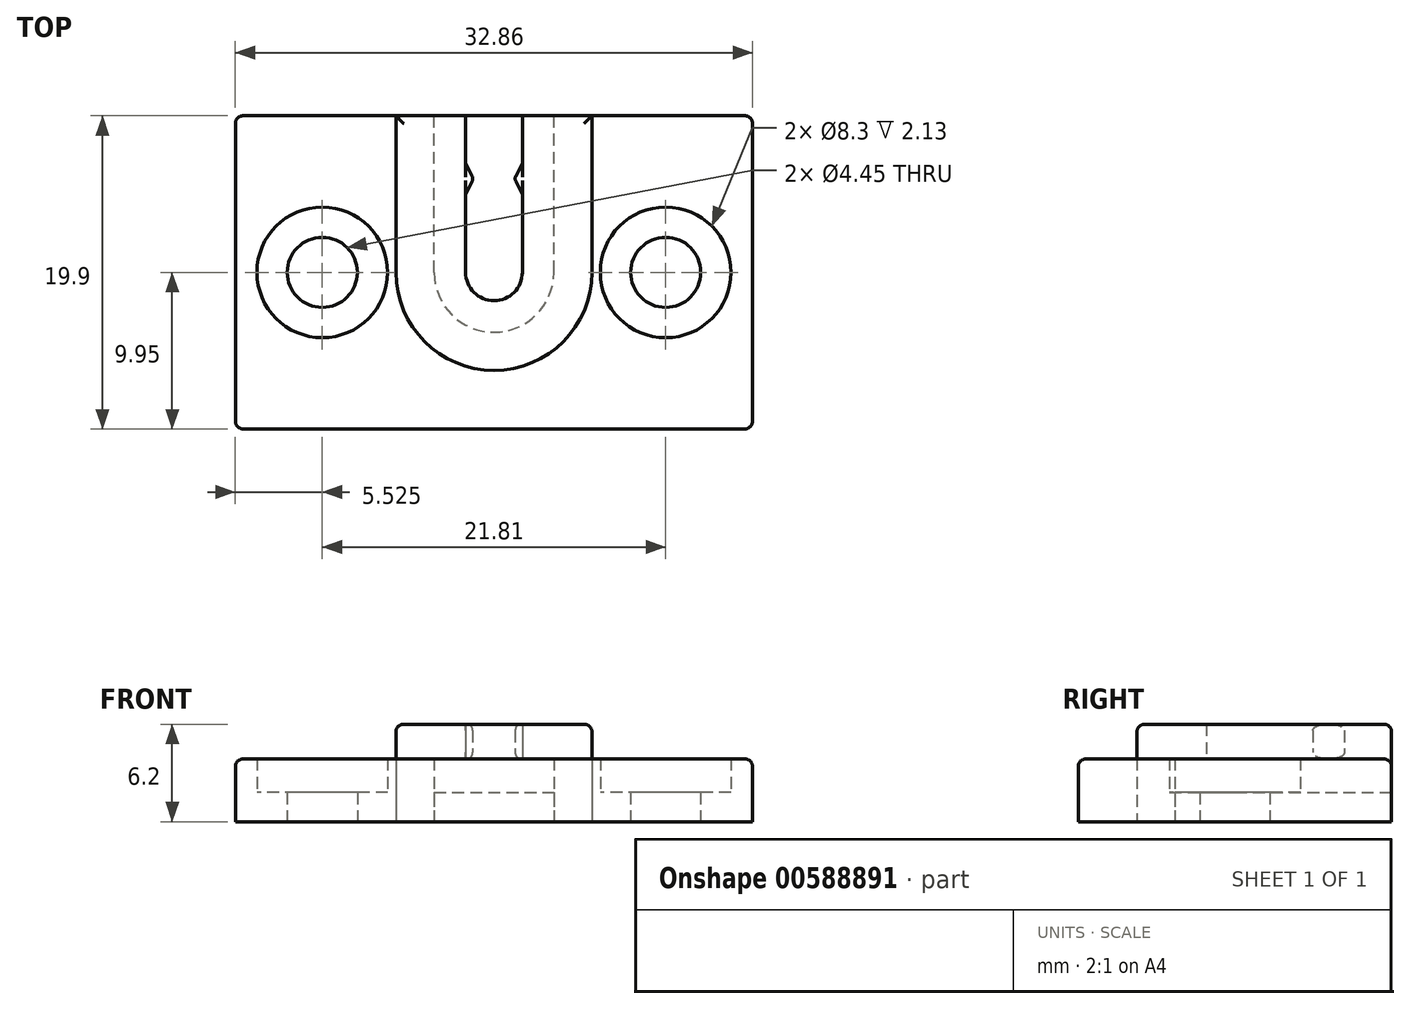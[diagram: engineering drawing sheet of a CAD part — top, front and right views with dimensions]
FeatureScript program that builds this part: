
annotation { "Feature Type Name" : "Feature", "Feature Type Description" : "" }
export const myFeature = defineFeature(function(context is Context, id is Id, definition is map)
    precondition{}
    {
        {
            var Q0;
            Q0=qCreatedBy(makeId("Top.planeOp"),FACE);
            var sketch = newSketch(context, id + "F0", { "sketchPlane" : qUnion([Q0])});
            skLineSegment(sketch, "E0.bottom", {"start": v(-16.43, 9.95) * mm, "end": v(16.43, 9.95) * mm});
            skLineSegment(sketch, "E0.top", {"start": v(-16.43, -9.95) * mm, "end": v(16.43, -9.95) * mm});
            skLineSegment(sketch, "E0.left", {"start": v(-16.43, 9.95) * mm, "end": v(-16.43, -9.95) * mm});
            skLineSegment(sketch, "E0.right", {"start": v(16.43, 9.95) * mm, "end": v(16.43, -9.95) * mm});
            skPoint(sketch, "E1", {"position": v(0, 9.95) * mm});
            skPoint(sketch, "E2", {"position": v(-16.43, 0) * mm});
            skLineSegment(sketch, "E3", {"start": v(-16.43, 9.95) * mm, "end": v(16.43, -9.95) * mm, "construction": true});
            skPoint(sketch, "E4", {"position": v(0, 0) * mm});
            skCircle(sketch, "E5", {"center": v(-10.9, 0) * mm, "radius": 4.15 * mm});
            skCircle(sketch, "E6", {"center": v(-10.9, 0) * mm, "radius": 2.23 * mm});
            skCircle(sketch, "E7", {"center": v(10.9, 0) * mm, "radius": 4.15 * mm});
            skLineSegment(sketch, "E8", {"start": v(-15.06, 0) * mm, "end": v(-16.43, 0) * mm, "construction": true});
            skLineSegment(sketch, "E9", {"start": v(16.43, 0) * mm, "end": v(15.06, 0) * mm, "construction": true});
            skCircle(sketch, "E10", {"center": v(10.9, 0) * mm, "radius": 2.23 * mm});
            skCircle(sketch, "E11", {"center": v(0, 0) * mm, "radius": 1.8 * mm});
            skCircle(sketch, "E12", {"center": v(0, 0) * mm, "radius": 6.22 * mm});
            skPoint(sketch, "E13", {"position": v(-6.22, 0) * mm});
            skPoint(sketch, "E14", {"position": v(6.22, 0) * mm});
            skPoint(sketch, "E15", {"position": v(-1.8, 0) * mm});
            skPoint(sketch, "E16", {"position": v(1.8, 0) * mm});
            skCircle(sketch, "E17", {"center": v(0, 0) * mm, "radius": 3.8 * mm});
            skPoint(sketch, "E18", {"position": v(-3.8, 0) * mm});
            skPoint(sketch, "E19", {"position": v(3.8, 0) * mm});
            skLineSegment(sketch, "E20", {"start": v(-6.22, 0) * mm, "end": v(-6.22, 9.95) * mm});
            skLineSegment(sketch, "E21", {"start": v(6.22, 0) * mm, "end": v(6.22, 9.95) * mm});
            skLineSegment(sketch, "E22", {"start": v(-3.8, 0) * mm, "end": v(-3.8, 9.95) * mm});
            skLineSegment(sketch, "E23", {"start": v(3.8, 0) * mm, "end": v(3.8, 9.95) * mm});
            skLineSegment(sketch, "E24", {"start": v(-1.8, 0) * mm, "end": v(-1.8, 9.95) * mm});
            skLineSegment(sketch, "E25", {"start": v(1.8, 0) * mm, "end": v(1.8, 9.95) * mm});
            skPoint(sketch, "E26", {"position": v(-1.8, 6.95) * mm});
            skPoint(sketch, "E27", {"position": v(-1.8, 4.95) * mm});
            skLineSegment(sketch, "E28", {"start": v(-1.8, 6.95) * mm, "end": v(-1.3, 5.95) * mm});
            skLineSegment(sketch, "E29", {"start": v(-1.3, 5.95) * mm, "end": v(-1.8, 4.95) * mm});
            skLineSegment(sketch, "E30", {"start": v(1.8, 6.95) * mm, "end": v(1.3, 5.95) * mm});
            skLineSegment(sketch, "E31", {"start": v(1.3, 5.95) * mm, "end": v(1.8, 4.95) * mm});
            skSolve(sketch);
        }
        {
            var Q0;
            Q0=makeQuery(id+"F0.imprint","IMPRINT",FACE,{"disambiguationData":[TD([[makeQuery(id+"F0.imprint","IMPRINT",EDGE,{"derivedFrom":sQuery(id+"F0.wireOp",EDGE,"E0.top")}),1.0]])]});
            extrude(context, id + "F1", {"entities" : qUnion([Q0]), "depth" : 4 * mm, "offsetDistance" : 25 * mm});
        }
        {
            var Q0;
            Q0=makeQuery(id+"F0.imprint","IMPRINT",FACE,{"disambiguationData":[TD([[makeQuery(id+"F0.imprint","IMPRINT",EDGE,{"derivedFrom":sQuery(id+"F0.wireOp",EDGE,"E5")}),1.0]])]});
            var Q1;
            Q1=makeQuery(id+"F0.imprint","IMPRINT",FACE,{"disambiguationData":[TD([[makeQuery(id+"F0.imprint","IMPRINT",EDGE,{"derivedFrom":sQuery(id+"F0.wireOp",EDGE,"E7")}),1.0]])]});
            var Q2;
            {var subQ0=sQuery(id+"F0.wireOp",EDGE,"E24");var subQ6=sQuery(id+"F0.wireOp",EDGE,"E12");var subQ8=makeQuery(id+"F0.imprint","INTERSECT",VERTEX,{"derivedFrom":[subQ6,subQ0]});Q2=makeQuery(id+"F0.imprint","IMPRINT",FACE,{"disambiguationData":[TD([[makeQuery(id+"F0.imprint","IMPRINT",EDGE,{"disambiguationData":[TD([[subQ8,-1.0]])],"derivedFrom":subQ6}),1.0]])]});}
            var Q3;
            {var subQ0=sQuery(id+"F0.wireOp",EDGE,"E24");var subQ1=sQuery(id+"F0.wireOp",EDGE,"E11");var subQ2=makeQuery(id+"F0.imprint","INTERSECT",VERTEX,{"derivedFrom":[subQ1,subQ0]});Q3=makeQuery(id+"F0.imprint","IMPRINT",FACE,{"disambiguationData":[TD([[makeQuery(id+"F0.imprint","IMPRINT",EDGE,{"disambiguationData":[TD([[subQ2,1.0]])],"derivedFrom":subQ1}),-1.0]])]});}
            var Q4;
            {var subQ3=sQuery(id+"F0.wireOp",EDGE,"E24");var subQ5=sQuery(id+"F0.wireOp",EDGE,"E11");var subQ6=makeQuery(id+"F0.imprint","INTERSECT",VERTEX,{"derivedFrom":[subQ5,subQ3]});Q4=makeQuery(id+"F0.imprint","IMPRINT",FACE,{"disambiguationData":[TD([[makeQuery(id+"F0.imprint","IMPRINT",EDGE,{"disambiguationData":[TD([[subQ6,-1.0]])],"derivedFrom":subQ5}),-1.0]])]});}
            var Q5;
            {var subQ0=sQuery(id+"F0.wireOp",EDGE,"E11");var subQ1=makeQuery(id+"F0.imprint","INTERSECT",VERTEX,{"derivedFrom":[subQ0,sQuery(id+"F0.wireOp",EDGE,"E24")]});Q5=makeQuery(id+"F0.imprint","IMPRINT",FACE,{"disambiguationData":[TD([[makeQuery(id+"F0.imprint","IMPRINT",EDGE,{"disambiguationData":[TD([[subQ1,1.0]])],"derivedFrom":subQ0}),1.0]])]});}
            var Q6;
            {var subQ4=sQuery(id+"F0.wireOp",EDGE,"E29");Q6=makeQuery(id+"F0.imprint","IMPRINT",FACE,{"disambiguationData":[TD([[makeQuery(id+"F0.imprint","IMPRINT",EDGE,{"derivedFrom":subQ4}),1.0]])]});}
            var Q7;
            {var subQ6=sQuery(id+"F0.wireOp",EDGE,"E0.bottom");var subQ9=sQuery(id+"F0.wireOp",EDGE,"E24");var subQ10=makeQuery(id+"F0.imprint","INTERSECT",VERTEX,{"derivedFrom":[subQ6,subQ9]});Q7=makeQuery(id+"F0.imprint","IMPRINT",FACE,{"disambiguationData":[TD([[makeQuery(id+"F0.imprint","IMPRINT",EDGE,{"disambiguationData":[TD([[subQ10,-1.0]])],"derivedFrom":subQ6}),-1.0]])]});}
            var Q8;
            {var subQ0=sQuery(id+"F0.wireOp",EDGE,"E22");var subQ1=sQuery(id+"F0.wireOp",EDGE,"E0.bottom");var subQ2=makeQuery(id+"F0.imprint","INTERSECT",VERTEX,{"derivedFrom":[subQ1,subQ0]});Q8=makeQuery(id+"F0.imprint","IMPRINT",FACE,{"disambiguationData":[TD([[makeQuery(id+"F0.imprint","IMPRINT",EDGE,{"disambiguationData":[TD([[subQ2,-1.0]])],"derivedFrom":subQ1}),-1.0]])]});}
            var Q9;
            {var subQ0=sQuery(id+"F0.wireOp",EDGE,"E23");var subQ1=sQuery(id+"F0.wireOp",EDGE,"E0.bottom");var subQ2=makeQuery(id+"F0.imprint","INTERSECT",VERTEX,{"derivedFrom":[subQ1,subQ0]});Q9=makeQuery(id+"F0.imprint","IMPRINT",FACE,{"disambiguationData":[TD([[makeQuery(id+"F0.imprint","IMPRINT",EDGE,{"disambiguationData":[TD([[subQ2,1.0]])],"derivedFrom":subQ1}),-1.0]])]});}
            var Q10;
            {var subQ4=sQuery(id+"F0.wireOp",EDGE,"E23");var subQ6=sQuery(id+"F0.wireOp",EDGE,"E12");var subQ7=makeQuery(id+"F0.imprint","INTERSECT",VERTEX,{"derivedFrom":[subQ6,subQ4]});Q10=makeQuery(id+"F0.imprint","IMPRINT",FACE,{"disambiguationData":[TD([[makeQuery(id+"F0.imprint","IMPRINT",EDGE,{"disambiguationData":[TD([[subQ7,-1.0]])],"derivedFrom":subQ6}),1.0]])]});}
            var Q11;
            {var subQ5=sQuery(id+"F0.wireOp",EDGE,"E31");Q11=makeQuery(id+"F0.imprint","IMPRINT",FACE,{"disambiguationData":[TD([[makeQuery(id+"F0.imprint","IMPRINT",EDGE,{"derivedFrom":subQ5}),1.0]])]});}
            var Q12;
            {var subQ0=sQuery(id+"F0.wireOp",EDGE,"E25");var subQ1=sQuery(id+"F0.wireOp",EDGE,"E12");var subQ2=makeQuery(id+"F0.imprint","INTERSECT",VERTEX,{"derivedFrom":[subQ1,subQ0]});Q12=makeQuery(id+"F0.imprint","IMPRINT",FACE,{"disambiguationData":[TD([[makeQuery(id+"F0.imprint","IMPRINT",EDGE,{"disambiguationData":[TD([[subQ2,-1.0]])],"derivedFrom":subQ1}),-1.0]])]});}
            var Q13;
            {var subQ0=sQuery(id+"F0.wireOp",EDGE,"E28");var subQ1=sQuery(id+"F0.wireOp",EDGE,"E12");var subQ2=makeQuery(id+"F0.imprint","INTERSECT",VERTEX,{"derivedFrom":[subQ1,subQ0]});Q13=makeQuery(id+"F0.imprint","IMPRINT",FACE,{"disambiguationData":[TD([[makeQuery(id+"F0.imprint","IMPRINT",EDGE,{"disambiguationData":[TD([[subQ2,-1.0]])],"derivedFrom":subQ1}),-1.0]])]});}
            var Q14;
            {var subQ5=sQuery(id+"F0.wireOp",EDGE,"E29");Q14=makeQuery(id+"F0.imprint","IMPRINT",FACE,{"disambiguationData":[TD([[makeQuery(id+"F0.imprint","IMPRINT",EDGE,{"derivedFrom":subQ5}),-1.0]])]});}
            extrude(context, id + "F2", {"entities" : qUnion([Q0, Q1, Q2, Q3, Q4, Q5, Q6, Q7, Q8, Q9, Q10, Q11, Q12, Q13, Q14]), "operationType" : NewBodyOperationType.ADD, "depth" : 1.87 * mm, "offsetDistance" : 25 * mm});
        }
        {
            var Q0;
            {var subQ0=sQuery(id+"F0.wireOp",EDGE,"E20");Q0=makeQuery(id+"F0.imprint","IMPRINT",FACE,{"disambiguationData":[TD([[makeQuery(id+"F0.imprint","IMPRINT",EDGE,{"derivedFrom":subQ0}),-1.0]])]});}
            var Q1;
            {var subQ0=sQuery(id+"F0.wireOp",EDGE,"E12");var subQ2=makeQuery(id+"F0.imprint","INTERSECT",VERTEX,{"derivedFrom":[subQ0,sQuery(id+"F0.wireOp",EDGE,"E21")]});Q1=makeQuery(id+"F0.imprint","IMPRINT",FACE,{"disambiguationData":[TD([[makeQuery(id+"F0.imprint","IMPRINT",EDGE,{"disambiguationData":[TD([[subQ2,-1.0]])],"derivedFrom":subQ0}),1.0]])]});}
            var Q2;
            {var subQ0=sQuery(id+"F0.wireOp",EDGE,"E21");Q2=makeQuery(id+"F0.imprint","IMPRINT",FACE,{"disambiguationData":[TD([[makeQuery(id+"F0.imprint","IMPRINT",EDGE,{"derivedFrom":subQ0}),1.0]])]});}
            extrude(context, id + "F3", {"entities" : qUnion([Q0, Q1, Q2]), "depth" : 6.2 * mm, "offsetDistance" : 25 * mm});
        }
        {
            var Q0;
            {var subQ0=sQuery(id+"F0.wireOp",EDGE,"E22");var subQ1=sQuery(id+"F0.wireOp",EDGE,"E0.bottom");var subQ2=makeQuery(id+"F0.imprint","INTERSECT",VERTEX,{"derivedFrom":[subQ1,subQ0]});Q0=makeQuery(id+"F0.imprint","IMPRINT",FACE,{"disambiguationData":[TD([[makeQuery(id+"F0.imprint","IMPRINT",EDGE,{"disambiguationData":[TD([[subQ2,-1.0]])],"derivedFrom":subQ1}),-1.0]])]});}
            var Q1;
            {var subQ0=sQuery(id+"F0.wireOp",EDGE,"E24");var subQ6=sQuery(id+"F0.wireOp",EDGE,"E12");var subQ8=makeQuery(id+"F0.imprint","INTERSECT",VERTEX,{"derivedFrom":[subQ6,subQ0]});Q1=makeQuery(id+"F0.imprint","IMPRINT",FACE,{"disambiguationData":[TD([[makeQuery(id+"F0.imprint","IMPRINT",EDGE,{"disambiguationData":[TD([[subQ8,-1.0]])],"derivedFrom":subQ6}),1.0]])]});}
            var Q2;
            {var subQ3=sQuery(id+"F0.wireOp",EDGE,"E24");var subQ5=sQuery(id+"F0.wireOp",EDGE,"E11");var subQ6=makeQuery(id+"F0.imprint","INTERSECT",VERTEX,{"derivedFrom":[subQ5,subQ3]});Q2=makeQuery(id+"F0.imprint","IMPRINT",FACE,{"disambiguationData":[TD([[makeQuery(id+"F0.imprint","IMPRINT",EDGE,{"disambiguationData":[TD([[subQ6,-1.0]])],"derivedFrom":subQ5}),-1.0]])]});}
            var Q3;
            {var subQ4=sQuery(id+"F0.wireOp",EDGE,"E23");var subQ6=sQuery(id+"F0.wireOp",EDGE,"E12");var subQ7=makeQuery(id+"F0.imprint","INTERSECT",VERTEX,{"derivedFrom":[subQ6,subQ4]});Q3=makeQuery(id+"F0.imprint","IMPRINT",FACE,{"disambiguationData":[TD([[makeQuery(id+"F0.imprint","IMPRINT",EDGE,{"disambiguationData":[TD([[subQ7,-1.0]])],"derivedFrom":subQ6}),1.0]])]});}
            var Q4;
            {var subQ0=sQuery(id+"F0.wireOp",EDGE,"E23");var subQ1=sQuery(id+"F0.wireOp",EDGE,"E0.bottom");var subQ2=makeQuery(id+"F0.imprint","INTERSECT",VERTEX,{"derivedFrom":[subQ1,subQ0]});Q4=makeQuery(id+"F0.imprint","IMPRINT",FACE,{"disambiguationData":[TD([[makeQuery(id+"F0.imprint","IMPRINT",EDGE,{"disambiguationData":[TD([[subQ2,1.0]])],"derivedFrom":subQ1}),-1.0]])]});}
            var Q5;
            {var subQ0=sQuery(id+"F0.wireOp",EDGE,"E28");var subQ1=sQuery(id+"F0.wireOp",EDGE,"E12");var subQ2=makeQuery(id+"F0.imprint","INTERSECT",VERTEX,{"derivedFrom":[subQ1,subQ0]});Q5=makeQuery(id+"F0.imprint","IMPRINT",FACE,{"disambiguationData":[TD([[makeQuery(id+"F0.imprint","IMPRINT",EDGE,{"disambiguationData":[TD([[subQ2,-1.0]])],"derivedFrom":subQ1}),-1.0]])]});}
            var Q6;
            {var subQ5=sQuery(id+"F0.wireOp",EDGE,"E29");Q6=makeQuery(id+"F0.imprint","IMPRINT",FACE,{"disambiguationData":[TD([[makeQuery(id+"F0.imprint","IMPRINT",EDGE,{"derivedFrom":subQ5}),-1.0]])]});}
            var Q7;
            {var subQ5=sQuery(id+"F0.wireOp",EDGE,"E31");Q7=makeQuery(id+"F0.imprint","IMPRINT",FACE,{"disambiguationData":[TD([[makeQuery(id+"F0.imprint","IMPRINT",EDGE,{"derivedFrom":subQ5}),1.0]])]});}
            var Q8;
            {var subQ0=sQuery(id+"F0.wireOp",EDGE,"E25");var subQ1=sQuery(id+"F0.wireOp",EDGE,"E12");var subQ2=makeQuery(id+"F0.imprint","INTERSECT",VERTEX,{"derivedFrom":[subQ1,subQ0]});Q8=makeQuery(id+"F0.imprint","IMPRINT",FACE,{"disambiguationData":[TD([[makeQuery(id+"F0.imprint","IMPRINT",EDGE,{"disambiguationData":[TD([[subQ2,-1.0]])],"derivedFrom":subQ1}),-1.0]])]});}
            extrude(context, id + "F4", {"entities" : qUnion([Q0, Q1, Q2, Q3, Q4, Q5, Q6, Q7, Q8]), "operationType" : NewBodyOperationType.ADD, "depth" : 6.2 * mm, "offsetDistance" : 25 * mm, "hasSecondDirection" : true, "secondDirectionOppositeDirection" : true, "secondDirectionDepth" : -4 * mm});
        }
        {
            var Q0;
            Q0=makeQuery(id+"F4.opExtrude","CAP_EDGE",EDGE,{"disambiguationData":[OSD([sQuery(id+"F0.wireOp",EDGE,"E30")])],"isStart":false});
            var Q1;
            Q1=makeQuery(id+"F4.opExtrude","CAP_EDGE",EDGE,{"disambiguationData":[OSD([sQuery(id+"F0.wireOp",EDGE,"E31")])],"isStart":false});
            var Q2;
            Q2=makeQuery(id+"F4.opExtrude","CAP_EDGE",EDGE,{"disambiguationData":[OSD([sQuery(id+"F0.wireOp",EDGE,"E29")])],"isStart":false});
            var Q3;
            Q3=makeQuery(id+"F4.opExtrude","CAP_EDGE",EDGE,{"disambiguationData":[OSD([sQuery(id+"F0.wireOp",EDGE,"E28")])],"isStart":false});
            var Q4;
            Q4=makeQuery(id+"F4.opExtrude","CAP_EDGE",EDGE,{"disambiguationData":[OSD([sQuery(id+"F0.wireOp",EDGE,"E28")])],"isStart":true});
            var Q5;
            Q5=makeQuery(id+"F4.opExtrude","CAP_EDGE",EDGE,{"disambiguationData":[OSD([sQuery(id+"F0.wireOp",EDGE,"E30")])],"isStart":true});
            var Q6;
            Q6=makeQuery(id+"F4.opExtrude","CAP_EDGE",EDGE,{"disambiguationData":[OSD([sQuery(id+"F0.wireOp",EDGE,"E29")])],"isStart":true});
            var Q7;
            Q7=makeQuery(id+"F4.opExtrude","CAP_EDGE",EDGE,{"disambiguationData":[OSD([sQuery(id+"F0.wireOp",EDGE,"E31")])],"isStart":true});
            var Q8;
            Q8=makeQuery(id+"F4.opExtrude","SWEPT_EDGE",EDGE,{"disambiguationData":[OSD([sQuery(id+"F0.wireOp",EDGE,"E28"),sQuery(id+"F0.wireOp",EDGE,"E29")])]});
            var Q9;
            Q9=makeQuery(id+"F4.opExtrude","SWEPT_EDGE",EDGE,{"disambiguationData":[OSD([sQuery(id+"F0.wireOp",EDGE,"E30"),sQuery(id+"F0.wireOp",EDGE,"E31")])]});
            fillet(context, id + "F5", {"entities" : qUnion([Q0, Q1, Q2, Q3, Q4, Q5, Q6, Q7, Q8, Q9]), "radius" : .4 * mm, "tangentPropagation" : true, "allowEdgeOverflow" : false});
        }
        {
            var Q0;
            Q0=makeQuery(id+"F1.opExtrude","CAP_EDGE",EDGE,{"disambiguationData":[OSD([sQuery(id+"F0.wireOp",EDGE,"E0.top")])],"isStart":false});
            var Q1;
            Q1=makeQuery(id+"F1.opExtrude","CAP_EDGE",EDGE,{"disambiguationData":[OSD([sQuery(id+"F0.wireOp",EDGE,"E0.right")])],"isStart":false});
            var Q2;
            Q2=makeQuery(id+"F1.opExtrude","CAP_EDGE",EDGE,{"disambiguationData":[OSD([sQuery(id+"F0.wireOp",EDGE,"E0.left")])],"isStart":false});
            var Q3;
            {var subQ0=sQuery(id+"F0.wireOp",EDGE,"E0.bottom");Q3=makeQuery(id+"F1.opExtrude","CAP_EDGE",EDGE,{"disambiguationData":[OSD([subQ0]),TDD([makeQuery(id+"F0.imprint","IMPRINT",EDGE,{"disambiguationData":[TD([[makeQuery(id+"F0.imprint","INTERSECT",VERTEX,{"derivedFrom":[subQ0,sQuery(id+"F0.wireOp",EDGE,"E0.left")]}),-1.0]])],"derivedFrom":subQ0})])],"isStart":false});}
            var Q4;
            {var subQ0=sQuery(id+"F0.wireOp",EDGE,"E0.bottom");Q4=makeQuery(id+"F1.opExtrude","CAP_EDGE",EDGE,{"disambiguationData":[OSD([subQ0]),TDD([makeQuery(id+"F0.imprint","IMPRINT",EDGE,{"disambiguationData":[TD([[makeQuery(id+"F0.imprint","INTERSECT",VERTEX,{"derivedFrom":[subQ0,sQuery(id+"F0.wireOp",EDGE,"E0.right")]}),1.0]])],"derivedFrom":subQ0})])],"isStart":false});}
            var Q5;
            Q5=makeQuery(id+"F1.opExtrude","SWEPT_EDGE",EDGE,{"disambiguationData":[OSD([sQuery(id+"F0.wireOp",EDGE,"E0.top"),sQuery(id+"F0.wireOp",EDGE,"E0.right")])]});
            var Q6;
            Q6=makeQuery(id+"F1.opExtrude","SWEPT_EDGE",EDGE,{"disambiguationData":[OSD([sQuery(id+"F0.wireOp",EDGE,"E0.top"),sQuery(id+"F0.wireOp",EDGE,"E0.left")])]});
            var Q7;
            Q7=makeQuery(id+"F1.opExtrude","SWEPT_EDGE",EDGE,{"disambiguationData":[OSD([sQuery(id+"F0.wireOp",EDGE,"E0.bottom"),sQuery(id+"F0.wireOp",EDGE,"E0.right")])]});
            var Q8;
            Q8=makeQuery(id+"F1.opExtrude","SWEPT_EDGE",EDGE,{"disambiguationData":[OSD([sQuery(id+"F0.wireOp",EDGE,"E0.bottom"),sQuery(id+"F0.wireOp",EDGE,"E0.left")])]});
            var Q9;
            {var subQ0=sQuery(id+"F0.wireOp",EDGE,"E0.bottom");var subQ1=makeQuery(id+"F0.imprint","INTERSECT",VERTEX,{"derivedFrom":[subQ0,sQuery(id+"F0.wireOp",EDGE,"E22")]});Q9=makeQuery(id+"F4.boolean.opBoolean","MERGE",EDGE,{"derivedFrom":[makeQuery(id+"F3.opExtrude","CAP_EDGE",EDGE,{"disambiguationData":[OSD([subQ0]),TDD([makeQuery(id+"F0.imprint","IMPRINT",EDGE,{"disambiguationData":[TD([[makeQuery(id+"F0.imprint","INTERSECT",VERTEX,{"derivedFrom":[subQ0,sQuery(id+"F0.wireOp",EDGE,"E20")]}),-1.0]])],"derivedFrom":subQ0})])],"isStart":false}),makeQuery(id+"F4.opExtrude","CAP_EDGE",EDGE,{"disambiguationData":[OSD([subQ0]),TDD([makeQuery(id+"F0.imprint","IMPRINT",EDGE,{"disambiguationData":[TD([[subQ1,-1.0]])],"derivedFrom":subQ0})])],"isStart":false})]});}
            var Q10;
            {var subQ0=sQuery(id+"F0.wireOp",EDGE,"E0.bottom");var subQ1=makeQuery(id+"F0.imprint","INTERSECT",VERTEX,{"derivedFrom":[subQ0,sQuery(id+"F0.wireOp",EDGE,"E23")]});Q10=makeQuery(id+"F4.boolean.opBoolean","MERGE",EDGE,{"derivedFrom":[makeQuery(id+"F3.opExtrude","CAP_EDGE",EDGE,{"disambiguationData":[OSD([subQ0]),TDD([makeQuery(id+"F0.imprint","IMPRINT",EDGE,{"disambiguationData":[TD([[makeQuery(id+"F0.imprint","INTERSECT",VERTEX,{"derivedFrom":[subQ0,sQuery(id+"F0.wireOp",EDGE,"E21")]}),1.0]])],"derivedFrom":subQ0})])],"isStart":false}),makeQuery(id+"F4.opExtrude","CAP_EDGE",EDGE,{"disambiguationData":[OSD([subQ0]),TDD([makeQuery(id+"F0.imprint","IMPRINT",EDGE,{"disambiguationData":[TD([[subQ1,1.0]])],"derivedFrom":subQ0})])],"isStart":false})]});}
            var Q11;
            Q11=makeQuery(id+"F3.opExtrude","CAP_EDGE",EDGE,{"disambiguationData":[OSD([sQuery(id+"F0.wireOp",EDGE,"E21")])],"isStart":false});
            fillet(context, id + "F6", {"entities" : qUnion([Q0, Q1, Q2, Q3, Q4, Q5, Q6, Q7, Q8, Q9, Q10, Q11]), "radius" : .5 * mm, "tangentPropagation" : true, "allowEdgeOverflow" : false});
        }
    });
